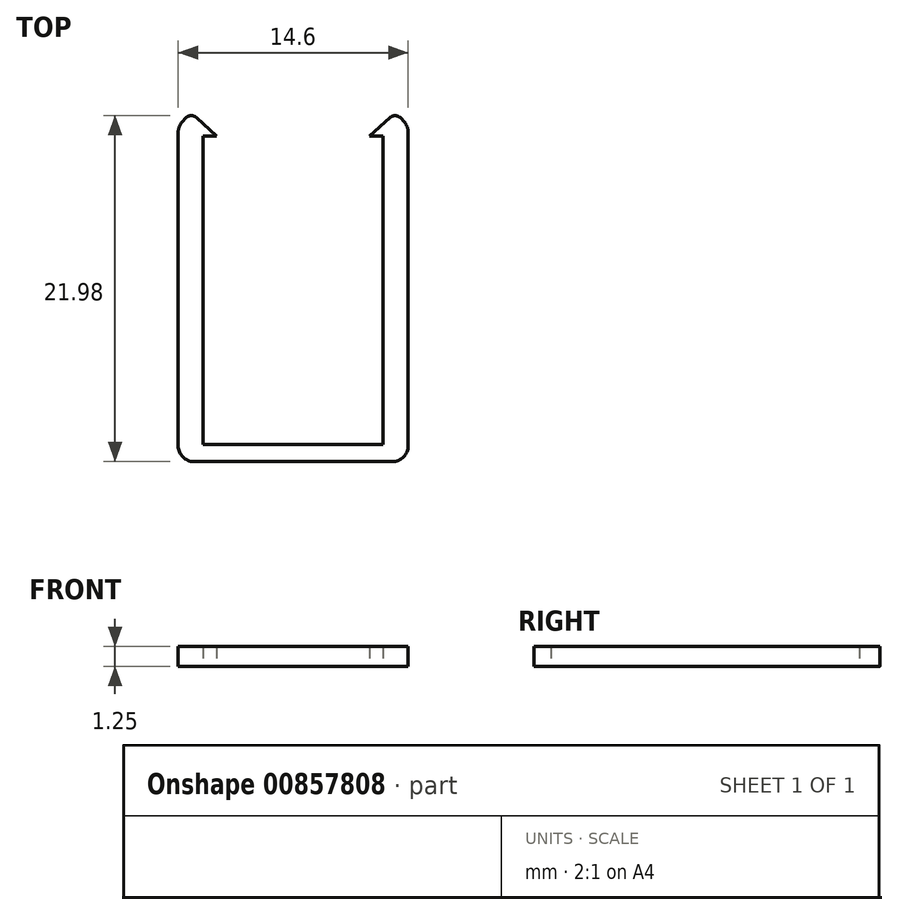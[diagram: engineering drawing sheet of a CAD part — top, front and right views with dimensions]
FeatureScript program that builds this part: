
annotation { "Feature Type Name" : "Feature", "Feature Type Description" : "" }
export const myFeature = defineFeature(function(context is Context, id is Id, definition is map)
    precondition{}
    {
        {
            var Q0;
            Q0=qCreatedBy(makeId("Top.planeOp"),FACE);
            var sketch = newSketch(context, id + "F0", { "sketchPlane" : qUnion([Q0])});
            skLineSegment(sketch, "E0.bottom", {"start": v(-7.97, -9.2) * mm, "end": v(6.63, -9.2) * mm});
            skLineSegment(sketch, "E0.top", {"start": v(-7.97, -10.28) * mm, "end": v(6.63, -10.28) * mm});
            skLineSegment(sketch, "E0.left", {"start": v(-7.97, -9.2) * mm, "end": v(-7.97, -10.28) * mm});
            skLineSegment(sketch, "E0.right", {"start": v(6.63, -9.2) * mm, "end": v(6.63, -10.28) * mm});
            skLineSegment(sketch, "E1.bottom", {"start": v(-7.97, -9.2) * mm, "end": v(-6.38, -9.2) * mm});
            skLineSegment(sketch, "E1.top", {"start": v(-7.97, 11.9) * mm, "end": v(-6.38, 11.9) * mm});
            skLineSegment(sketch, "E1.left", {"start": v(-7.97, -9.2) * mm, "end": v(-7.97, 11.9) * mm});
            skLineSegment(sketch, "E1.right", {"start": v(-6.38, -9.2) * mm, "end": v(-6.38, 11.9) * mm});
            skLineSegment(sketch, "E2.bottom", {"start": v(6.63, -9.2) * mm, "end": v(5.04, -9.2) * mm});
            skLineSegment(sketch, "E2.top", {"start": v(6.63, 11.9) * mm, "end": v(5.04, 11.9) * mm});
            skLineSegment(sketch, "E2.left", {"start": v(6.63, -9.2) * mm, "end": v(6.63, 11.9) * mm});
            skLineSegment(sketch, "E2.right", {"start": v(5.04, -9.2) * mm, "end": v(5.04, 11.9) * mm});
            skPoint(sketch, "E3", {"position": v(-6.38, 10.4) * mm});
            skPoint(sketch, "E4", {"position": v(5.04, 10.4) * mm});
            skPoint(sketch, "E5", {"position": v(-5.53, 10.4) * mm});
            skPoint(sketch, "E6", {"position": v(4.2, 10.4) * mm});
            skPoint(sketch, "E7", {"position": v(-7.17, 11.9) * mm});
            skPoint(sketch, "E8", {"position": v(5.84, 11.9) * mm});
            skLineSegment(sketch, "E9", {"start": v(-7.17, 11.9) * mm, "end": v(-5.53, 10.4) * mm});
            skLineSegment(sketch, "E10", {"start": v(5.84, 11.9) * mm, "end": v(4.2, 10.4) * mm});
            skLineSegment(sketch, "E11", {"start": v(4.2, 10.4) * mm, "end": v(5.04, 10.4) * mm});
            skLineSegment(sketch, "E12", {"start": v(-5.53, 10.4) * mm, "end": v(-6.38, 10.4) * mm});
            skLineSegment(sketch, "E13", {"start": v(-7.17, 11.9) * mm, "end": v(-7.97, 11.03) * mm});
            skLineSegment(sketch, "E14", {"start": v(5.84, 11.9) * mm, "end": v(6.63, 11.03) * mm});
            skSolve(sketch);
        }
        {
            var Q0;
            {var subQ6=sQuery(id+"F0.wireOp",EDGE,"E13");Q0=makeQuery(id+"F0.imprint","IMPRINT",FACE,{"disambiguationData":[TD([[makeQuery(id+"F0.imprint","IMPRINT",EDGE,{"derivedFrom":subQ6}),1.0]])]});}
            var Q1;
            {var subQ3=sQuery(id+"F0.wireOp",EDGE,"E12");Q1=makeQuery(id+"F0.imprint","IMPRINT",FACE,{"disambiguationData":[TD([[makeQuery(id+"F0.imprint","IMPRINT",EDGE,{"derivedFrom":subQ3}),-1.0]])]});}
            var Q2;
            {var subQ3=sQuery(id+"F0.wireOp",EDGE,"E11");Q2=makeQuery(id+"F0.imprint","IMPRINT",FACE,{"disambiguationData":[TD([[makeQuery(id+"F0.imprint","IMPRINT",EDGE,{"derivedFrom":subQ3}),1.0]])]});}
            var Q3;
            {var subQ7=sQuery(id+"F0.wireOp",EDGE,"E14");Q3=makeQuery(id+"F0.imprint","IMPRINT",FACE,{"disambiguationData":[TD([[makeQuery(id+"F0.imprint","IMPRINT",EDGE,{"derivedFrom":subQ7}),-1.0]])]});}
            var Q4;
            Q4=makeQuery(id+"F0.imprint","IMPRINT",FACE,{"disambiguationData":[TD([[makeQuery(id+"F0.imprint","IMPRINT",EDGE,{"derivedFrom":sQuery(id+"F0.wireOp",EDGE,"E0.top")}),1.0]])]});
            extrude(context, id + "F1", {"entities" : qUnion([Q0, Q1, Q2, Q3, Q4]), "depth" : 1.25 * mm, "offsetDistance" : 25 * mm});
        }
        {
            var Q0;
            Q0=makeQuery(id+"F1.opExtrude","SWEPT_EDGE",EDGE,{"disambiguationData":[OSD([sQuery(id+"F0.wireOp",EDGE,"E0.top"),sQuery(id+"F0.wireOp",EDGE,"E0.right")])]});
            var Q1;
            Q1=makeQuery(id+"F1.opExtrude","SWEPT_EDGE",EDGE,{"disambiguationData":[OSD([sQuery(id+"F0.wireOp",EDGE,"E0.top"),sQuery(id+"F0.wireOp",EDGE,"E0.left")])]});
            fillet(context, id + "F2", {"entities" : qUnion([Q0, Q1]), "radius" : 1 * mm, "tangentPropagation" : true, "allowEdgeOverflow" : false});
        }
        {
            var Q0;
            Q0=makeQuery(id+"F1.opExtrude","SWEPT_EDGE",EDGE,{"disambiguationData":[OSD([sQuery(id+"F0.wireOp",EDGE,"E1.left"),sQuery(id+"F0.wireOp",EDGE,"E13")])]});
            var Q1;
            Q1=makeQuery(id+"F1.opExtrude","SWEPT_EDGE",EDGE,{"disambiguationData":[OSD([sQuery(id+"F0.wireOp",EDGE,"E2.left"),sQuery(id+"F0.wireOp",EDGE,"E14")])]});
            fillet(context, id + "F3", {"entities" : qUnion([Q0, Q1]), "radius" : 1 * mm, "tangentPropagation" : true, "allowEdgeOverflow" : false});
        }
        {
            var Q0;
            Q0=makeQuery(id+"F1.opExtrude","SWEPT_EDGE",EDGE,{"disambiguationData":[OSD([sQuery(id+"F0.wireOp",EDGE,"E2.top"),sQuery(id+"F0.wireOp",EDGE,"E10"),sQuery(id+"F0.wireOp",EDGE,"E14")])]});
            var Q1;
            Q1=makeQuery(id+"F1.opExtrude","SWEPT_EDGE",EDGE,{"disambiguationData":[OSD([sQuery(id+"F0.wireOp",EDGE,"E1.top"),sQuery(id+"F0.wireOp",EDGE,"E9"),sQuery(id+"F0.wireOp",EDGE,"E13")])]});
            fillet(context, id + "F4", {"entities" : qUnion([Q0, Q1]), "radius" : 0.5 * mm, "tangentPropagation" : true, "allowEdgeOverflow" : false});
        }
    });
